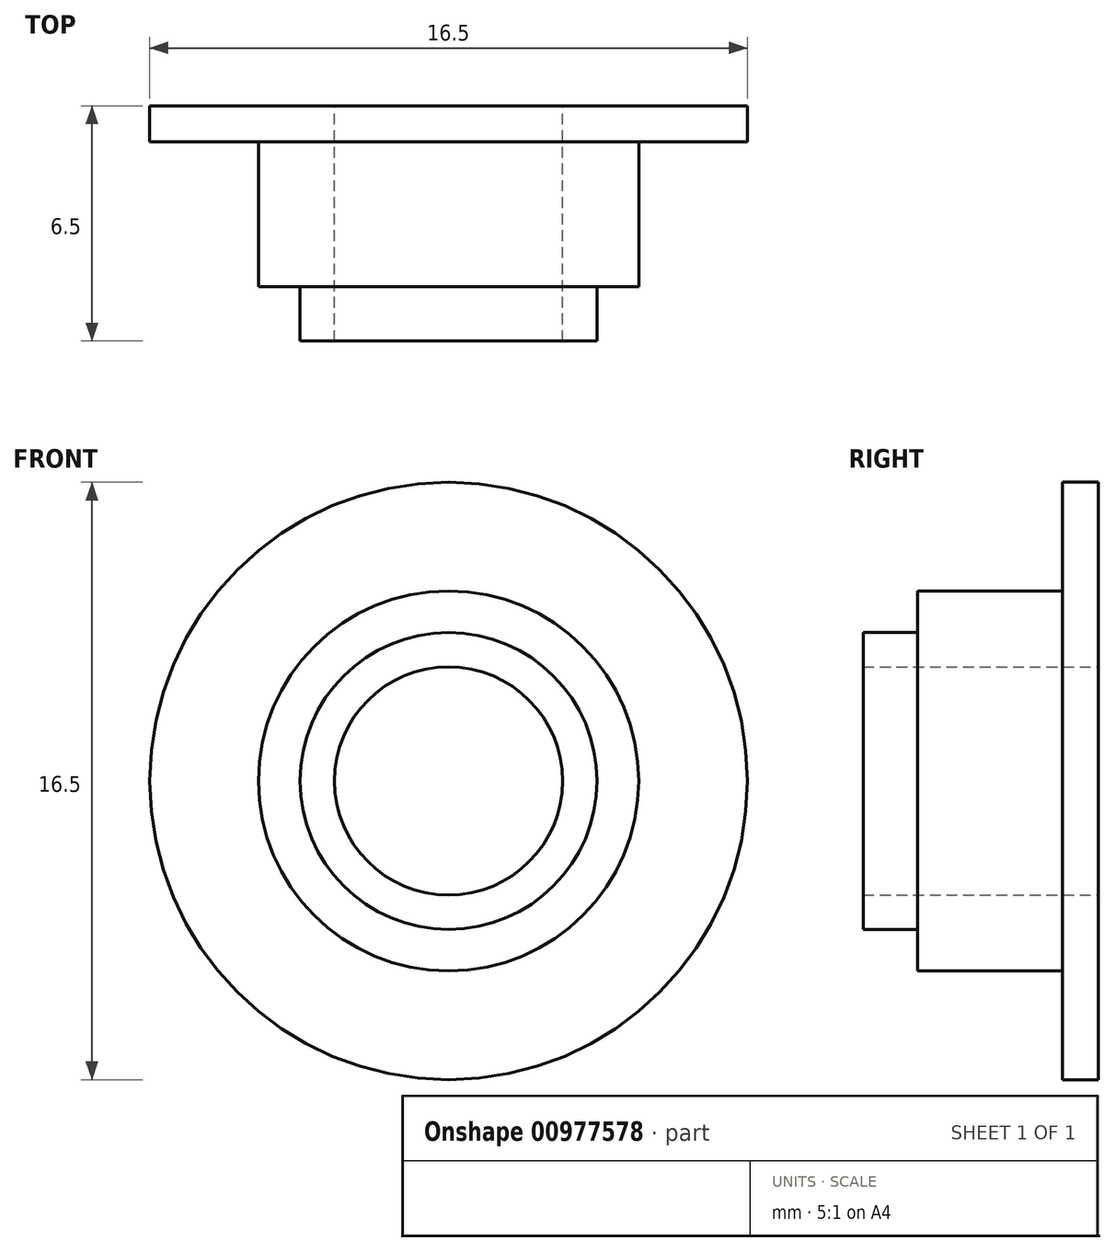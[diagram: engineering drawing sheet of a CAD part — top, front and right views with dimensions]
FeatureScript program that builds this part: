
annotation { "Feature Type Name" : "Feature", "Feature Type Description" : "" }
export const myFeature = defineFeature(function(context is Context, id is Id, definition is map)
    precondition{}
    {
        {
            var Q0;
            Q0=qCreatedBy(makeId("Front.planeOp"),FACE);
            var sketch = newSketch(context, id + "F0", { "sketchPlane" : qUnion([Q0])});
            skCircle(sketch, "E0", {"center": v(0, 0) * mm, "radius": 5.25 * mm});
            skCircle(sketch, "E1.0", {"center": v(0, 0) * mm, "radius": 8.25 * mm});
            skCircle(sketch, "E2", {"center": v(0, 0) * mm, "radius": 3.15 * mm});
            skCircle(sketch, "E3", {"center": v(0, 0) * mm, "radius": 4.1 * mm});
            skSolve(sketch);
        }
        {
            var Q0;
            Q0=makeQuery(id+"F0.imprint","IMPRINT",FACE,{"disambiguationData":[TD([[makeQuery(id+"F0.imprint","IMPRINT",EDGE,{"derivedFrom":sQuery(id+"F0.wireOp",EDGE,"E0")}),-1.0]])]});
            extrude(context, id + "F1", {"entities" : qUnion([Q0]), "depth" : 1 * mm, "offsetDistance" : 25 * mm});
        }
        {
            var Q0;
            Q0=makeQuery(id+"F0.imprint","IMPRINT",FACE,{"disambiguationData":[TD([[makeQuery(id+"F0.imprint","IMPRINT",EDGE,{"derivedFrom":sQuery(id+"F0.wireOp",EDGE,"E0")}),1.0]])]});
            extrude(context, id + "F2", {"entities" : qUnion([Q0]), "operationType" : NewBodyOperationType.ADD, "flatOperationType" : FlatOperationType.REMOVE, "depth" : 5 * mm, "offsetDistance" : 25 * mm, "domain" : OperationDomain.MODEL});
        }
        {
            var Q0;
            Q0=makeQuery(id+"F0.imprint","IMPRINT",FACE,{"disambiguationData":[TD([[makeQuery(id+"F0.imprint","IMPRINT",EDGE,{"derivedFrom":sQuery(id+"F0.wireOp",EDGE,"E2")}),-1.0]])]});
            extrude(context, id + "F3", {"entities" : qUnion([Q0]), "operationType" : NewBodyOperationType.ADD, "flatOperationType" : FlatOperationType.REMOVE, "depth" : 6.5 * mm, "offsetDistance" : 25 * mm, "domain" : OperationDomain.MODEL});
        }
    });
